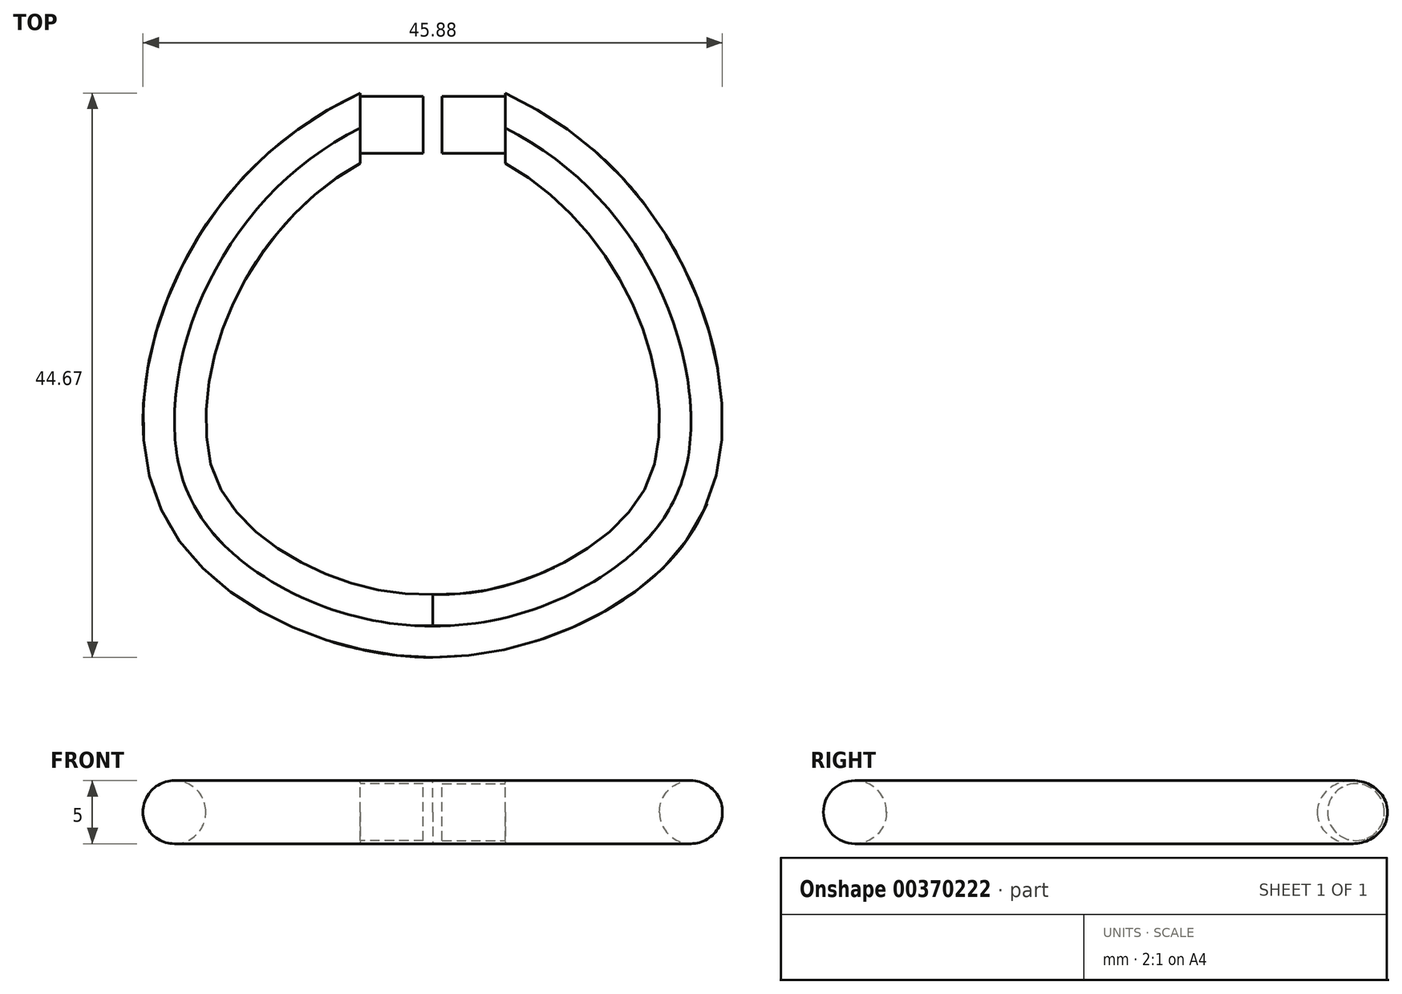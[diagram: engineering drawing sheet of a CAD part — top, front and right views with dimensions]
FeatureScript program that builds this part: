
annotation { "Feature Type Name" : "Feature", "Feature Type Description" : "" }
export const myFeature = defineFeature(function(context is Context, id is Id, definition is map)
    precondition{}
    {
        {
            var Q0;
            Q0=qCreatedBy(makeId("Top.planeOp"),FACE);
            var sketch = newSketch(context, id + "F0", { "sketchPlane" : qUnion([Q0])});
            skFitSpline(sketch, "E0", {"points": [v(-5.75, 25.48) * mm, v(-18.4, 14.34) * mm, v(-22.94, 0) * mm, v(-18.56, -11.8) * mm, v(0, -19.2) * mm], "startDerivative": vector(-65.2, -30.34) * mm, "endDerivative": vector(76.66, 0) * mm});
            skFitSpline(sketch, "E1.0", {"points": [v(-3.64, 20.95) * mm, v(-4.79, 20.42) * mm, v(-6.92, 19.23) * mm, v(-9.67, 17.13) * mm, v(-12.03, 14.74) * mm, v(-14.03, 12.04) * mm, v(-15.69, 9.06) * mm, v(-16.94, 5.93) * mm, v(-17.6, 3.32) * mm, v(-17.87, 1.3) * mm, v(-17.96, -0.16) * mm, v(-17.92, -1.54) * mm, v(-17.72, -3.26) * mm, v(-17.27, -4.8) * mm, v(-16.58, -6.22) * mm, v(-16.02, -7.08) * mm, v(-15.48, -7.76) * mm, v(-15.03, -8.26) * mm, v(-14.52, -8.76) * mm, v(-13.76, -9.44) * mm, v(-12.67, -10.27) * mm, v(-10.65, -11.53) * mm, v(-7.74, -12.88) * mm, v(-3.88, -13.94) * mm, v(-1.27, -14.2) * mm, v(0, -14.2) * mm]});
            skLineSegment(sketch, "E2", {"start": v(-5.75, 25.48) * mm, "end": v(-5.75, 19.85) * mm});
            skFitSpline(sketch, "E3.MirrorCS", {"points": [v(5.75, 25.48) * mm, v(18.4, 14.34) * mm, v(22.94, 0) * mm, v(18.56, -11.8) * mm, v(0, -19.2) * mm], "startDerivative": vector(65.2, -30.34) * mm, "endDerivative": vector(-76.66, 0) * mm});
            skLineSegment(sketch, "E4.MirrorCS", {"start": v(5.75, 25.48) * mm, "end": v(5.75, 19.85) * mm});
            skLineSegment(sketch, "E5", {"start": v(0, -19.2) * mm, "end": v(-7.14, -19.2) * mm, "construction": true});
            skFitSpline(sketch, "E6.0", {"points": [v(3.64, 20.95) * mm, v(4.79, 20.42) * mm, v(6.92, 19.23) * mm, v(9.67, 17.13) * mm, v(12.03, 14.74) * mm, v(14.03, 12.04) * mm, v(15.69, 9.06) * mm, v(16.94, 5.93) * mm, v(17.6, 3.32) * mm, v(17.87, 1.3) * mm, v(17.96, -0.16) * mm, v(17.92, -1.54) * mm, v(17.72, -3.26) * mm, v(17.27, -4.8) * mm, v(16.58, -6.22) * mm, v(16.02, -7.08) * mm, v(15.48, -7.76) * mm, v(15.03, -8.26) * mm, v(14.52, -8.76) * mm, v(13.76, -9.44) * mm, v(12.67, -10.27) * mm, v(10.65, -11.53) * mm, v(7.74, -12.88) * mm, v(3.88, -13.94) * mm, v(1.27, -14.2) * mm, v(0, -14.2) * mm], "construction": true});
            skPoint(sketch, "E7", {"position": v(5.75, 19.85) * mm});
            skFitSpline(sketch, "E8", {"points": [v(3.64, 20.95) * mm, v(4.79, 20.42) * mm, v(6.92, 19.23) * mm, v(9.67, 17.13) * mm, v(12.03, 14.74) * mm, v(14.03, 12.04) * mm, v(15.69, 9.06) * mm, v(16.94, 5.93) * mm, v(17.6, 3.32) * mm, v(17.87, 1.3) * mm, v(17.96, -0.16) * mm, v(17.92, -1.54) * mm, v(17.72, -3.26) * mm, v(17.27, -4.8) * mm, v(16.58, -6.22) * mm, v(16.02, -7.08) * mm, v(15.48, -7.76) * mm, v(15.03, -8.26) * mm, v(14.52, -8.76) * mm, v(13.76, -9.44) * mm, v(12.67, -10.27) * mm, v(10.65, -11.53) * mm, v(7.74, -12.88) * mm, v(3.88, -13.94) * mm, v(1.27, -14.2) * mm, v(0, -14.2) * mm]});
            skLineSegment(sketch, "E9", {"start": v(0, -14.2) * mm, "end": v(-0.2, -14.2) * mm});
            skSolve(sketch);
        }
        {
            var Q0;
            Q0 = qSketchRegion(id + "F0", true);
            extrude(context, id + "F1", {"entities" : qUnion([Q0]), "depth" : 5 * mm});
        }
        {
            var Q0;
            Q0=makeQuery(id+"F1.opExtrude","SWEPT_FACE",FACE,{"disambiguationData":[OSD([sQuery(id+"F0.wireOp",EDGE,"E2")])]});
            var sketch = newSketch(context, id + "F2", { "sketchPlane" : qUnion([Q0])});
            skCircle(sketch, "E10", {"center": v(22.98, 2.5) * mm, "radius": 2.25 * mm});
            skSolve(sketch);
        }
        {
            var Q0;
            Q0=makeQuery(id+"F1.opExtrude","SWEPT_FACE",FACE,{"disambiguationData":[OSD([sQuery(id+"F0.wireOp",EDGE,"E4.MirrorCS")])]});
            var sketch = newSketch(context, id + "F3", { "sketchPlane" : qUnion([Q0])});
            skCircle(sketch, "E11", {"center": v(-22.98, 2.5) * mm, "radius": 2.25 * mm});
            skSolve(sketch);
        }
        {
            var Q0;
            Q0=makeQuery(id+"F1.opExtrude","CAP_EDGE",EDGE,{"disambiguationData":[OSD([sQuery(id+"F0.wireOp",EDGE,"E1.0")])],"isStart":true});
            var Q1;
            Q1=makeQuery(id+"F1.opExtrude","CAP_EDGE",EDGE,{"disambiguationData":[OSD([sQuery(id+"F0.wireOp",EDGE,"E9")])],"isStart":true});
            var Q2;
            Q2=makeQuery(id+"F1.opExtrude","CAP_EDGE",EDGE,{"disambiguationData":[OSD([sQuery(id+"F0.wireOp",EDGE,"E1.0")])],"isStart":false});
            var Q3;
            Q3=makeQuery(id+"F1.opExtrude","CAP_EDGE",EDGE,{"disambiguationData":[OSD([sQuery(id+"F0.wireOp",EDGE,"E9")])],"isStart":false});
            var Q4;
            Q4=makeQuery(id+"F1.opExtrude","CAP_EDGE",EDGE,{"disambiguationData":[OSD([sQuery(id+"F0.wireOp",EDGE,"E8")])],"isStart":false});
            var Q5;
            Q5=makeQuery(id+"F1.opExtrude","CAP_EDGE",EDGE,{"disambiguationData":[OSD([sQuery(id+"F0.wireOp",EDGE,"E8")])],"isStart":true});
            var Q6;
            Q6=makeQuery(id+"F1.opExtrude","CAP_EDGE",EDGE,{"disambiguationData":[OSD([sQuery(id+"F0.wireOp",EDGE,"E3.MirrorCS")])],"isStart":true});
            var Q7;
            Q7=makeQuery(id+"F1.opExtrude","CAP_EDGE",EDGE,{"disambiguationData":[OSD([sQuery(id+"F0.wireOp",EDGE,"E3.MirrorCS")])],"isStart":false});
            var Q8;
            Q8=makeQuery(id+"F1.opExtrude","CAP_EDGE",EDGE,{"disambiguationData":[OSD([sQuery(id+"F0.wireOp",EDGE,"E0")])],"isStart":false});
            var Q9;
            Q9=makeQuery(id+"F1.opExtrude","CAP_EDGE",EDGE,{"disambiguationData":[OSD([sQuery(id+"F0.wireOp",EDGE,"E0")])],"isStart":true});
            fillet(context, id + "F4", {"entities" : qUnion([Q0, Q1, Q2, Q3, Q4, Q5, Q6, Q7, Q8, Q9]), "radius" : 2.5 * mm, "tangentPropagation" : true, "allowEdgeOverflow" : false});
        }
        {
            var Q0;
            Q0 = qSketchRegion(id + "F2", true);
            extrude(context, id + "F5", {"entities" : qUnion([Q0]), "operationType" : NewBodyOperationType.ADD, "depth" : 5 * mm});
        }
        {
            var Q0;
            Q0 = qSketchRegion(id + "F3", true);
            extrude(context, id + "F6", {"entities" : qUnion([Q0]), "operationType" : NewBodyOperationType.ADD, "depth" : 5 * mm});
        }
    });
